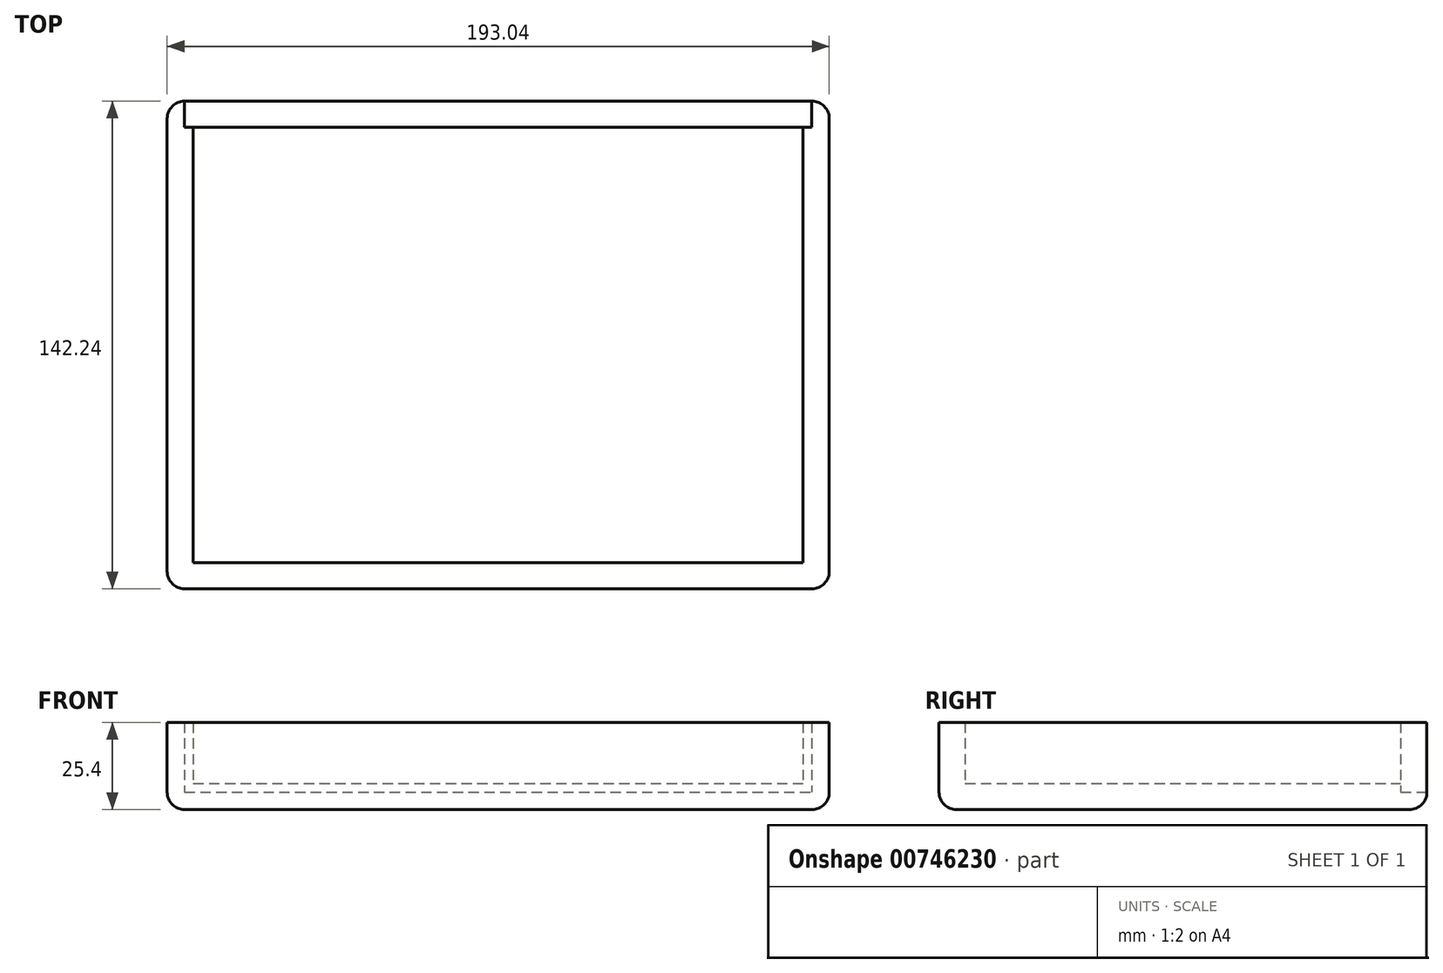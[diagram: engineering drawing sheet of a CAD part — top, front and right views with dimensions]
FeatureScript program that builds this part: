
annotation { "Feature Type Name" : "Feature", "Feature Type Description" : "" }
export const myFeature = defineFeature(function(context is Context, id is Id, definition is map)
    precondition{}
    {
        {
            var Q0;
            Q0=qCreatedBy(makeId("Top.planeOp"),FACE);
            var sketch = newSketch(context, id + "F0", { "sketchPlane" : qUnion([Q0])});
            skLineSegment(sketch, "E0.bottom", {"start": v(-93.3, -53.46) * mm, "end": v(99.75, -53.46) * mm});
            skLineSegment(sketch, "E0.top", {"start": v(-93.3, 88.78) * mm, "end": v(99.75, 88.78) * mm});
            skLineSegment(sketch, "E0.left", {"start": v(-93.3, -53.46) * mm, "end": v(-93.3, 88.78) * mm});
            skLineSegment(sketch, "E0.right", {"start": v(99.75, -53.46) * mm, "end": v(99.75, 88.78) * mm});
            skSolve(sketch);
        }
        {
            var Q0;
            Q0=makeQuery(id+"F0.imprint","IMPRINT",FACE,{"disambiguationData":[TD([[makeQuery(id+"F0.imprint","IMPRINT",EDGE,{"derivedFrom":sQuery(id+"F0.wireOp",EDGE,"E0.bottom")}),1.0]])]});
            extrude(context, id + "F1", {"entities" : qUnion([Q0]), "depth" : 25.4 * mm, "offsetDistance" : 25.4 * mm});
        }
        {
            var Q0;
            Q0=makeQuery(id+"F1.opExtrude","CAP_FACE",FACE,{"disambiguationData":[OSD([sQuery(id+"F0.wireOp",EDGE,"E0.bottom"),sQuery(id+"F0.wireOp",EDGE,"E0.top"),sQuery(id+"F0.wireOp",EDGE,"E0.left"),sQuery(id+"F0.wireOp",EDGE,"E0.right")])],"isStart":false});
            shell(context, id + "F2", {"entities" : qUnion([Q0]), "thickness" : 7.62 * mm});
        }
        {
            var Q0;
            Q0=makeQuery(id+"F1.opExtrude","SWEPT_EDGE",EDGE,{"disambiguationData":[OSD([sQuery(id+"F0.wireOp",EDGE,"E0.bottom"),sQuery(id+"F0.wireOp",EDGE,"E0.left")])]});
            var Q1;
            Q1=makeQuery(id+"F1.opExtrude","SWEPT_EDGE",EDGE,{"disambiguationData":[OSD([sQuery(id+"F0.wireOp",EDGE,"E0.top"),sQuery(id+"F0.wireOp",EDGE,"E0.left")])]});
            var Q2;
            Q2=makeQuery(id+"F1.opExtrude","SWEPT_EDGE",EDGE,{"disambiguationData":[OSD([sQuery(id+"F0.wireOp",EDGE,"E0.top"),sQuery(id+"F0.wireOp",EDGE,"E0.right")])]});
            var Q3;
            Q3=makeQuery(id+"F1.opExtrude","SWEPT_EDGE",EDGE,{"disambiguationData":[OSD([sQuery(id+"F0.wireOp",EDGE,"E0.bottom"),sQuery(id+"F0.wireOp",EDGE,"E0.right")])]});
            var Q4;
            Q4=makeQuery(id+"F1.opExtrude","CAP_EDGE",EDGE,{"disambiguationData":[OSD([sQuery(id+"F0.wireOp",EDGE,"E0.top")])],"isStart":true});
            var Q5;
            Q5=makeQuery(id+"F1.opExtrude","CAP_EDGE",EDGE,{"disambiguationData":[OSD([sQuery(id+"F0.wireOp",EDGE,"E0.right")])],"isStart":true});
            var Q6;
            Q6=makeQuery(id+"F1.opExtrude","CAP_EDGE",EDGE,{"disambiguationData":[OSD([sQuery(id+"F0.wireOp",EDGE,"E0.bottom")])],"isStart":true});
            var Q7;
            Q7=makeQuery(id+"F1.opExtrude","CAP_EDGE",EDGE,{"disambiguationData":[OSD([sQuery(id+"F0.wireOp",EDGE,"E0.left")])],"isStart":true});
            fillet(context, id + "F3", {"entities" : qUnion([Q0, Q1, Q2, Q3, Q4, Q5, Q6, Q7]), "radius" : 5.08 * mm, "tangentPropagation" : true, "allowEdgeOverflow" : false});
        }
        {
            var Q0;
            Q0=makeQuery(id+"F1.opExtrude","SWEPT_FACE",FACE,{"disambiguationData":[OSD([sQuery(id+"F0.wireOp",EDGE,"E0.top")])]});
            extrude(context, id + "F4", {"entities" : qUnion([Q0]), "operationType" : NewBodyOperationType.REMOVE, "oppositeDirection" : true, "depth" : 7.62 * mm, "offsetDistance" : 25.4 * mm});
        }
    });
